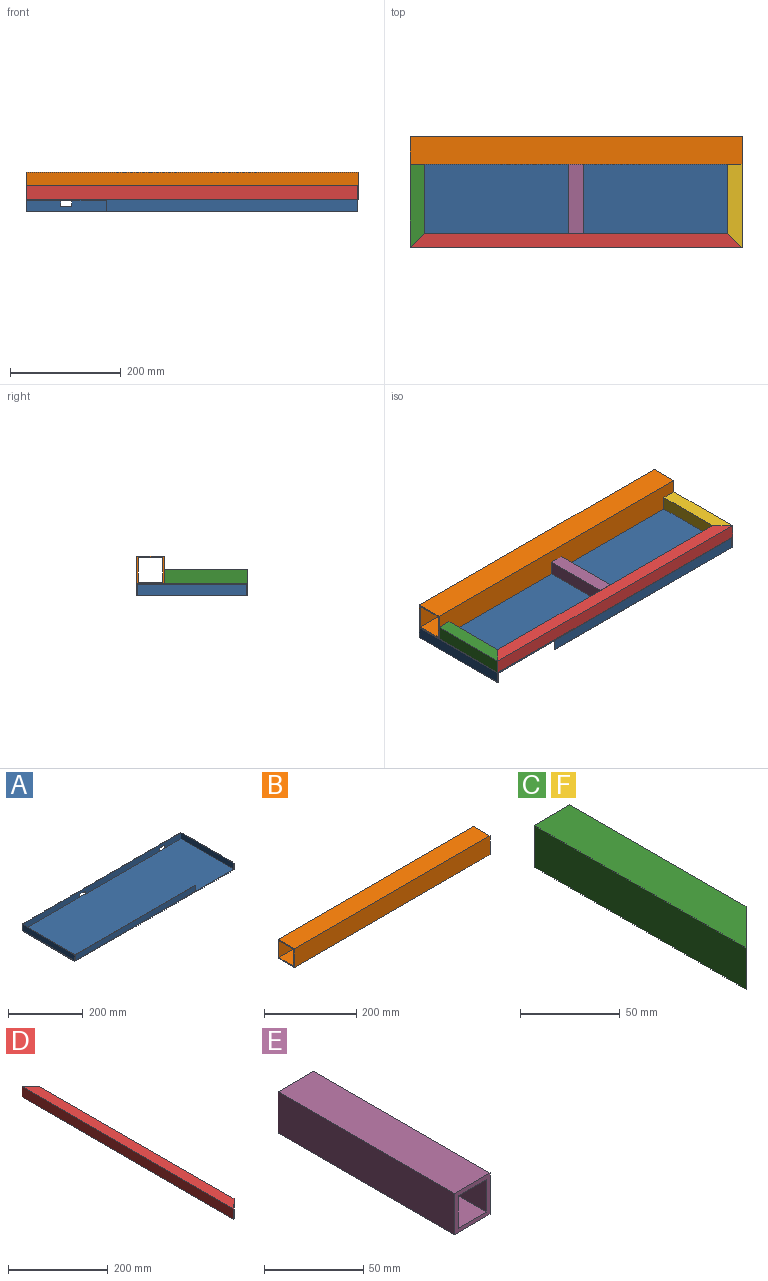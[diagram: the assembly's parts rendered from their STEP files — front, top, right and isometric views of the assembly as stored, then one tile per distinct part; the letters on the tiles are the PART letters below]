
ASSEMBLY  parts=6 mates=8
PART A: 19 faces, bbox 600x200x22 mm
  f0: plane 600x22mm, normal (0,1,0), area 12800mm2, adj f3,f4,f5,f9,f10,f13,f14,f15
  f1: plane 598.16x20mm, normal (0,-1,0), area 11563.2mm2, adj f7,f8,f9,f10,f13,f14,f15,f16
  f2: plane 600x22mm, normal (0,-1,0), area 10318.4mm2, adj f3,f4,f5,f9,f10,f11,f12
  f3: plane 200x22mm, normal (1,0,0), area 4400mm2, adj f0,f2,f5,f9
  f4: plane 200x22mm, normal (-1,0,0), area 4400mm2, adj f0,f2,f5,f9
  f5: plane 600x200mm, normal (0,0,-1), area 120000mm2, adj f0,f2,f3,f4
  f6: plane 454.08x20mm, normal (0,1,0), area 9081.6mm2, adj f7,f9,f10,f12
  f7: plane 198.16x20mm, normal (1,0,0), area 3963.2mm2, adj f1,f6,f9,f10
  f8: plane 198.16x20mm, normal (-1,0,0), area 3963.2mm2, adj f1,f9,f10,f11
  f9: plane 600x200mm, normal (0,0,1), area 1334.9mm2, adj f0,f1,f2,f3,f4,f6,f7,f8
  f10: plane 598.16x200mm, normal (0,0,1), area 118701.9mm2, adj f0,f1,f2,f6,f7,f8,f11,f12
  f11: plane 20x0.92mm, normal (-1,0,0), area 18.4mm2, adj f2,f8,f9,f10
  f12: plane 20x0.92mm, normal (1,0,0), area 18.4mm2, adj f2,f6,f9,f10
  f13: plane 20x0.92mm, normal (0,0,-1), area 18.4mm2, adj f0,f1,f14,f15
  f14: plane 10x0.92mm, normal (1,0,0), area 9.2mm2, adj f0,f1,f10,f13
  f15: plane 10x0.92mm, normal (-1,0,0), area 9.2mm2, adj f0,f1,f10,f13
  f16: plane 20x0.92mm, normal (0,0,-1), area 18.4mm2, adj f0,f1,f17,f18
  f17: plane 10x0.92mm, normal (-1,0,0), area 9.2mm2, adj f0,f1,f10,f16
  f18: plane 10x0.92mm, normal (1,0,0), area 9.2mm2, adj f0,f1,f10,f16
PART B: 10 faces, bbox 600x50x50 mm
  f0: plane 600x45mm, normal (0,1,0), area 27000mm2, adj f1,f7,f8,f9
  f1: plane 600x45mm, normal (0,0,-1), area 27000mm2, adj f0,f2,f8,f9
  f2: plane 600x45mm, normal (0,-1,0), area 27000mm2, adj f1,f7,f8,f9
  f3: plane 600x50mm, normal (0,0,1), area 30000mm2, adj f4,f6,f8,f9
  f4: plane 600x50mm, normal (0,-1,0), area 30000mm2, adj f3,f5,f8,f9
  f5: plane 600x50mm, normal (0,0,-1), area 30000mm2, adj f4,f6,f8,f9
  f6: plane 600x50mm, normal (0,1,0), area 30000mm2, adj f3,f5,f8,f9
  f7: plane 600x45mm, normal (0,0,1), area 27000mm2, adj f0,f2,f8,f9
  f8: plane 50x50mm, normal (-1,0,0), area 475mm2, adj f0,f1,f2,f3,f4,f5,f6,f7
  f9: plane 50x50mm, normal (1,0,0), area 475mm2, adj f0,f1,f2,f3,f4,f5,f6,f7
PART C: 10 faces, bbox 25.4x150x25.4 mm
  f0: plane 150x25.4mm, normal (0,0,1), area 3487.4mm2, adj f1,f7,f8,f9
  f1: plane 124.6x25.4mm, normal (1,0,0), area 3164.8mm2, adj f0,f5,f8,f9
  f2: plane 147.3x20mm, normal (1,0,0), area 2946mm2, adj f3,f6,f8,f9
  f3: plane 147.3x20mm, normal (0,0,-1), area 2746mm2, adj f2,f4,f8,f9
  f4: plane 127.3x20mm, normal (-1,0,0), area 2546mm2, adj f3,f6,f8,f9
  f5: plane 150x25.4mm, normal (0,0,-1), area 3487.4mm2, adj f1,f7,f8,f9
  f6: plane 147.3x20mm, normal (0,0,1), area 2746mm2, adj f2,f4,f8,f9
  f7: plane 150x25.4mm, normal (-1,0,0), area 3810mm2, adj f0,f5,f8,f9
  f8: plane 25.4x25.4mm, normal (0,1,0), area 245.2mm2, adj f0,f1,f2,f3,f4,f5,f6,f7
  f9: plane 25.4x25.4mm, normal (0.71,-0.71,0), area 346.7mm2, adj f0,f1,f2,f3,f4,f5,f6,f7
PART D: 10 faces, bbox 25.4x600x25.4 mm
  f0: plane 594.6x20mm, normal (0,0,1), area 11492mm2, adj f1,f3,f4,f5
  f1: plane 554.6x20mm, normal (-1,0,0), area 11092mm2, adj f0,f2,f4,f5
  f2: plane 594.6x20mm, normal (0,0,-1), area 11492mm2, adj f1,f3,f4,f5
  f3: plane 594.6x20mm, normal (1,0,0), area 11892mm2, adj f0,f2,f4,f5
  f4: plane 25.4x25.4mm, normal (0.71,0.71,0), area 346.7mm2, adj f0,f1,f2,f3,f6,f7,f8,f9
  f5: plane 25.4x25.4mm, normal (0.71,-0.71,0), area 346.7mm2, adj f0,f1,f2,f3,f6,f7,f8,f9
  f6: plane 600x25.4mm, normal (0,0,1), area 14594.8mm2, adj f4,f5,f7,f9
  f7: plane 549.2x25.4mm, normal (1,0,0), area 13949.7mm2, adj f4,f5,f6,f8
  f8: plane 600x25.4mm, normal (0,0,-1), area 14594.8mm2, adj f4,f5,f7,f9
  f9: plane 600x25.4mm, normal (-1,0,0), area 15240mm2, adj f4,f5,f6,f8
PART E: 10 faces, bbox 25.4x125.5x25.4 mm
  f0: plane 125.5x20mm, normal (1,0,0), area 2510mm2, adj f1,f7,f8,f9
  f1: plane 125.5x20mm, normal (0,0,-1), area 2510mm2, adj f0,f2,f8,f9
  f2: plane 125.5x20mm, normal (-1,0,0), area 2510mm2, adj f1,f7,f8,f9
  f3: plane 125.5x25.4mm, normal (0,0,1), area 3187.7mm2, adj f4,f6,f8,f9
  f4: plane 125.5x25.4mm, normal (-1,0,0), area 3187.7mm2, adj f3,f5,f8,f9
  f5: plane 125.5x25.4mm, normal (0,0,-1), area 3187.7mm2, adj f4,f6,f8,f9
  f6: plane 125.5x25.4mm, normal (1,0,0), area 3187.7mm2, adj f3,f5,f8,f9
  f7: plane 125.5x20mm, normal (0,0,1), area 2510mm2, adj f0,f2,f8,f9
  f8: plane 25.4x25.4mm, normal (0,-1,0), area 245.2mm2, adj f0,f1,f2,f3,f4,f5,f6,f7
  f9: plane 25.4x25.4mm, normal (0,1,0), area 245.2mm2, adj f0,f1,f2,f3,f4,f5,f6,f7
PART F: same geometry as C
PLACE A rot(axis=(0,-1,0),180deg) t=(-286.65,-134.01,-85.28)mm
PLACE B rot(axis=(1,0,0),180deg) t=(13.35,-59.01,-60.28)mm
PLACE C t=(-573.95,-84.01,-72.58)mm
PLACE D rot(axis=(0,0,1),90deg) t=(-586.65,-221.31,-72.58)mm
PLACE E t=(-286.65,-83.11,-72.58)mm
PLACE F rot(axis=(0,-1,0),180deg) t=(0.65,-84.01,-72.58)mm
MATE parallel A.f0 <-> B.f4  axis (0,1,0) through (-284.23,-34.01,-96.4)mm
MATE parallel E.f8 <-> D.f7  axis (0,-1,0) through (-286.65,-208.61,-72.58)mm
MATE parallel F.f8 <-> B.f6  axis (0,1,0) through (13.35,-84.01,-85.28)mm
MATE parallel A.f5 <-> F.f0  axis (0,0,1) through (13.35,-234.01,-85.28)mm
MATE parallel E.f8 <-> D.f7  axis (0,-1,0) through (-286.65,-208.61,-72.58)mm
MATE parallel C.f8 <-> B.f6  axis (0,1,0) through (-586.65,-84.01,-85.28)mm
MATE parallel D.f5 <-> F.f9  axis (0.71,0.71,0) through (0.65,-221.31,-72.58)mm
MATE parallel A.f5 <-> E.f5  axis (0,0,1) through (-286.65,-134.01,-85.28)mm
